FCSTD DOCUMENT  (FreeCAD 0.22RUnknown)
Label: board
License: All rights reserved
LicenseURL: http://en.wikipedia.org/wiki/All_rights_reserved
objects: Sketcher::SketchObject×1
note: 1 computed .brp shape members not serialized (recipe doc carries the construction recipe); baked Part::Feature solids carry a one-line shape summary decoded from their .brp

FEATURE [Sketcher::SketchObject] Sketch
  FullyConstrained = true
  sketch-geometry (62):
    g0: LineSegment StartX=0 StartY=0 StartZ=0 EndX=640 EndY=0 EndZ=0
    g1: LineSegment StartX=640 StartY=0 StartZ=0 EndX=640 EndY=-480 EndZ=0
    g2: LineSegment StartX=640 StartY=-480 StartZ=0 EndX=0 EndY=-480 EndZ=0
    g3: LineSegment StartX=0 StartY=-480 StartZ=0 EndX=0 EndY=0 EndZ=0
    g4: LineSegment StartX=96 StartY=-16 StartZ=0 EndX=152 EndY=-16 EndZ=0
    g5: LineSegment StartX=152 StartY=-16 StartZ=0 EndX=152 EndY=-72 EndZ=0
    g6: LineSegment StartX=152 StartY=-72 StartZ=0 EndX=96 EndY=-72 EndZ=0
    g7: LineSegment StartX=96 StartY=-72 StartZ=0 EndX=96 EndY=-16 EndZ=0
    g8: LineSegment StartX=152 StartY=-72 StartZ=0 EndX=208 EndY=-72 EndZ=0
    g9: LineSegment StartX=208 StartY=-72 StartZ=0 EndX=208 EndY=-128 EndZ=0
    g10: LineSegment StartX=208 StartY=-128 StartZ=0 EndX=152 EndY=-128 EndZ=0
    g11: LineSegment StartX=152 StartY=-128 StartZ=0 EndX=152 EndY=-72 EndZ=0
    g12: LineSegment StartX=208 StartY=-128 StartZ=0 EndX=264 EndY=-128 EndZ=0
    g13: LineSegment StartX=264 StartY=-128 StartZ=0 EndX=264 EndY=-184 EndZ=0
    g14: LineSegment StartX=264 StartY=-184 StartZ=0 EndX=208 EndY=-184 EndZ=0
    g15: LineSegment StartX=208 StartY=-184 StartZ=0 EndX=208 EndY=-128 EndZ=0
    g16: LineSegment StartX=264 StartY=-184 StartZ=0 EndX=320 EndY=-184 EndZ=0
    g17: LineSegment StartX=320 StartY=-184 StartZ=0 EndX=320 EndY=-240 EndZ=0
    g18: LineSegment StartX=320 StartY=-240 StartZ=0 EndX=264 EndY=-240 EndZ=0
    g19: LineSegment StartX=264 StartY=-240 StartZ=0 EndX=264 EndY=-184 EndZ=0
    g20: LineSegment StartX=320 StartY=-240 StartZ=0 EndX=376 EndY=-240 EndZ=0
    g21: LineSegment StartX=376 StartY=-240 StartZ=0 EndX=376 EndY=-296 EndZ=0
    g22: LineSegment StartX=376 StartY=-296 StartZ=0 EndX=320 EndY=-296 EndZ=0
    g23: LineSegment StartX=320 StartY=-296 StartZ=0 EndX=320 EndY=-240 EndZ=0
    g24: LineSegment StartX=376 StartY=-296 StartZ=0 EndX=432 EndY=-296 EndZ=0
    g25: LineSegment StartX=432 StartY=-296 StartZ=0 EndX=432 EndY=-352 EndZ=0
    g26: LineSegment StartX=432 StartY=-352 StartZ=0 EndX=376 EndY=-352 EndZ=0
    g27: LineSegment StartX=376 StartY=-352 StartZ=0 EndX=376 EndY=-296 EndZ=0
    g28: LineSegment StartX=432 StartY=-352 StartZ=0 EndX=488 EndY=-352 EndZ=0
    g29: LineSegment StartX=488 StartY=-352 StartZ=0 EndX=488 EndY=-408 EndZ=0
    g30: LineSegment StartX=488 StartY=-408 StartZ=0 EndX=432 EndY=-408 EndZ=0
    g31: LineSegment StartX=432 StartY=-408 StartZ=0 EndX=432 EndY=-352 EndZ=0
    g32: LineSegment StartX=488 StartY=-408 StartZ=0 EndX=544 EndY=-408 EndZ=0
    g33: LineSegment StartX=544 StartY=-408 StartZ=0 EndX=544 EndY=-464 EndZ=0
    g34: LineSegment StartX=544 StartY=-464 StartZ=0 EndX=488 EndY=-464 EndZ=0
    g35: LineSegment StartX=488 StartY=-464 StartZ=0 EndX=488 EndY=-408 EndZ=0
    g36: LineSegment StartX=96 StartY=-16 StartZ=0 EndX=0 EndY=-16 EndZ=0
    g37: LineSegment StartX=544 StartY=-464 StartZ=0 EndX=640 EndY=-464 EndZ=0
    g38: LineSegment StartX=96 StartY=-16 StartZ=0 EndX=96 EndY=0 EndZ=0
    g39: LineSegment StartX=544 StartY=-464 StartZ=0 EndX=544 EndY=-480 EndZ=0
    g40: LineSegment StartX=96 StartY=-16 StartZ=0 EndX=544 EndY=-464 EndZ=0
    g41: LineSegment StartX=96 StartY=-72 StartZ=0 EndX=152 EndY=-16 EndZ=0
    g42: LineSegment StartX=152 StartY=-128 StartZ=0 EndX=208 EndY=-72 EndZ=0
    g43: LineSegment StartX=208 StartY=-184 StartZ=0 EndX=264 EndY=-128 EndZ=0
    g44: LineSegment StartX=264 StartY=-240 StartZ=0 EndX=320 EndY=-184 EndZ=0
    g45: LineSegment StartX=320 StartY=-296 StartZ=0 EndX=376 EndY=-240 EndZ=0
    g46: LineSegment StartX=376 StartY=-352 StartZ=0 EndX=432 EndY=-296 EndZ=0
    g47: LineSegment StartX=432 StartY=-408 StartZ=0 EndX=488 EndY=-352 EndZ=0
    g48: LineSegment StartX=488 StartY=-464 StartZ=0 EndX=544 EndY=-408 EndZ=0
    g49: GeomPoint X=124 Y=-44 Z=0
    g50: GeomPoint X=180 Y=-100 Z=0
    g51: GeomPoint X=236 Y=-156 Z=0
    g52: GeomPoint X=292 Y=-212 Z=0
    g53: GeomPoint X=348 Y=-268 Z=0
    g54: GeomPoint X=404 Y=-324 Z=0
    g55: GeomPoint X=460 Y=-380 Z=0
    g56: GeomPoint X=516 Y=-436 Z=0
    g57: LineSegment StartX=96 StartY=-16 StartZ=0 EndX=544 EndY=-16 EndZ=0
    g58: LineSegment StartX=544 StartY=-16 StartZ=0 EndX=544 EndY=-408 EndZ=0
    g59: LineSegment StartX=488 StartY=-464 StartZ=0 EndX=96 EndY=-464 EndZ=0
    g60: LineSegment StartX=96 StartY=-464 StartZ=0 EndX=96 EndY=-72 EndZ=0
    g61: LineSegment StartX=96 StartY=-464 StartZ=0 EndX=544 EndY=-16 EndZ=0
  constraints (163):
    c: Coincident(g0,g1)
    c: Coincident(g1,g2)
    c: Coincident(g2,g3)
    c: Coincident(g3,g0)
    c: Horizontal(g0)
    c: Horizontal(g2)
    c: Vertical(g1)
    c: Vertical(g3)
    c: Coincident(g0,g-1)
    c: DistanceY(g3,g3) = 480
    c: DistanceX(g0,g0) = 640
    c: Coincident(g4,g5)
    c: Coincident(g5,g6)
    c: Coincident(g6,g7)
    c: Coincident(g7,g4)
    c: Horizontal(g4)
    c: Horizontal(g6)
    c: Vertical(g5)
    c: Vertical(g7)
    c: Coincident(g8,g9)
    c: Coincident(g9,g10)
    c: Coincident(g10,g11)
    c: Coincident(g11,g8)
    c: Horizontal(g8)
    c: Horizontal(g10)
    c: Vertical(g9)
    c: Vertical(g11)
    c: Coincident(g8,g5)
    c: Coincident(g12,g13)
    c: Coincident(g13,g14)
    c: Coincident(g14,g15)
    c: Coincident(g15,g12)
    c: Horizontal(g12)
    c: Horizontal(g14)
    c: Vertical(g13)
    c: Vertical(g15)
    c: Coincident(g12,g9)
    c: Coincident(g16,g17)
    c: Coincident(g17,g18)
    c: Coincident(g18,g19)
    c: Coincident(g19,g16)
    c: Horizontal(g16)
    c: Horizontal(g18)
    c: Vertical(g17)
    c: Vertical(g19)
    c: Coincident(g16,g13)
    c: Coincident(g20,g21)
    c: Coincident(g21,g22)
    c: Coincident(g22,g23)
    c: Coincident(g23,g20)
    c: Horizontal(g20)
    c: Horizontal(g22)
    c: Vertical(g21)
    c: Vertical(g23)
    c: Coincident(g20,g17)
    c: Coincident(g24,g25)
    c: Coincident(g25,g26)
    c: Coincident(g26,g27)
    c: Coincident(g27,g24)
    c: Horizontal(g24)
    c: Horizontal(g26)
    c: Vertical(g25)
    c: Vertical(g27)
    c: Coincident(g24,g21)
    c: Coincident(g28,g29)
    c: Coincident(g29,g30)
    c: Coincident(g30,g31)
    c: Coincident(g31,g28)
    c: Horizontal(g28)
    c: Horizontal(g30)
    c: Vertical(g29)
    c: Vertical(g31)
    c: Coincident(g28,g25)
    c: Coincident(g32,g33)
    c: Coincident(g33,g34)
    c: Coincident(g34,g35)
    c: Coincident(g35,g32)
    c: Horizontal(g32)
    c: Horizontal(g34)
    c: Vertical(g33)
    c: Vertical(g35)
    c: Coincident(g32,g29)
    c: Equal(g5,g6)
    c: Equal(g7,g8)
    c: Equal(g8,g9)
    c: Equal(g11,g12)
    c: Equal(g12,g13)
    c: Equal(g15,g16)
    c: Equal(g16,g17)
    c: Equal(g19,g20)
    c: Equal(g20,g21)
    c: Equal(g23,g24)
    c: Equal(g24,g25)
    c: Equal(g27,g28)
    c: Equal(g28,g29)
    c: Equal(g31,g32)
    c: Equal(g32,g33)
    c: Coincident(g36,g4)
    c: PointOnObject(g36,g3)
    c: Horizontal(g36)
    c: Coincident(g37,g33)
    c: PointOnObject(g37,g1)
    c: Horizontal(g37)
    c: Equal(g37,g36)
    c: Coincident(g38,g4)
    c: PointOnObject(g38,g0)
    c: Coincident(g39,g33)
    c: PointOnObject(g39,g2)
    c: Vertical(g39)
    c: Vertical(g38)
    c: Equal(g38,g39)
    c: Coincident(g40,g4)
    c: Coincident(g40,g33)
    c: Coincident(g41,g6)
    c: Coincident(g41,g4)
    c: Coincident(g42,g10)
    c: Coincident(g42,g8)
    c: Coincident(g43,g14)
    c: Coincident(g43,g12)
    c: Coincident(g44,g18)
    c: Coincident(g44,g16)
    c: Coincident(g45,g22)
    c: Coincident(g45,g20)
    c: Coincident(g46,g26)
    c: Coincident(g46,g24)
    c: Coincident(g47,g30)
    c: Coincident(g47,g28)
    c: Coincident(g48,g34)
    c: Coincident(g48,g32)
    c: PointOnObject(g50,g40)
    c: PointOnObject(g51,g40)
    c: PointOnObject(g52,g40)
    c: PointOnObject(g53,g45)
    c: PointOnObject(g54,g46)
    c: PointOnObject(g55,g47)
    c: PointOnObject(g56,g48)
    c: PointOnObject(g56,g40)
    c: PointOnObject(g55,g40)
    c: PointOnObject(g54,g40)
    c: PointOnObject(g53,g40)
    c: PointOnObject(g52,g44)
    c: PointOnObject(g51,g43)
    c: PointOnObject(g50,g42)
    c: PointOnObject(g49,g40)
    c: PointOnObject(g49,g41)
    c: Distance(g49,g3) = 124
    c: Distance(g49,g0) = 44
    c: Distance(g5) = 56
    c: DistanceY(g33,g4) = 448
    c: DistanceX(g4,g32) = 448
    c: Coincident(g57,g4)
    c: Horizontal(g57)
    c: Coincident(g58,g57)
    c: Coincident(g58,g32)
    c: Vertical(g58)
    c: Coincident(g59,g34)
    c: Horizontal(g59)
    c: Coincident(g60,g59)
    c: Coincident(g60,g6)
    c: Vertical(g60)
    c: Coincident(g61,g59)
    c: Coincident(g61,g57)
    c: DistanceX(g49,g17) = 196
